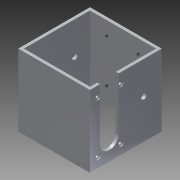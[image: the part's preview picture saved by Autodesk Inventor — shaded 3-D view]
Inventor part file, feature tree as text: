
AUTODESK INVENTOR PART (.ipt)
format: ipt  version: 2013 (Build 170138000, 138)  size: 169,984 bytes
history: native  units: mm
features: thread x4, sketch x4, hole x3, other x1, extrude x1
ambient origin geometry x1: Origin
feature tree (13):
  other  "ソリッド1"
  extrude  "押し出し1"  Depth=50.0mm
  hole  "穴1"  [1 undecoded]
  hole  "穴6"  [1 undecoded]
  hole  "穴12"  [1 undecoded]
  thread  "ねじ1"
  thread  "ねじ2"
  thread  "ねじ3"
  thread  "ねじ4"
  sketch  "スケッチ1"
  sketch  "スケッチ3"
  sketch  "スケッチ11"
  sketch  "スケッチ17"
note: 3 required parameter values undecoded (feature->parameter linkage not recoverable at this tier; creation-order binding heuristic only, values carry confidence <= 0.55)
